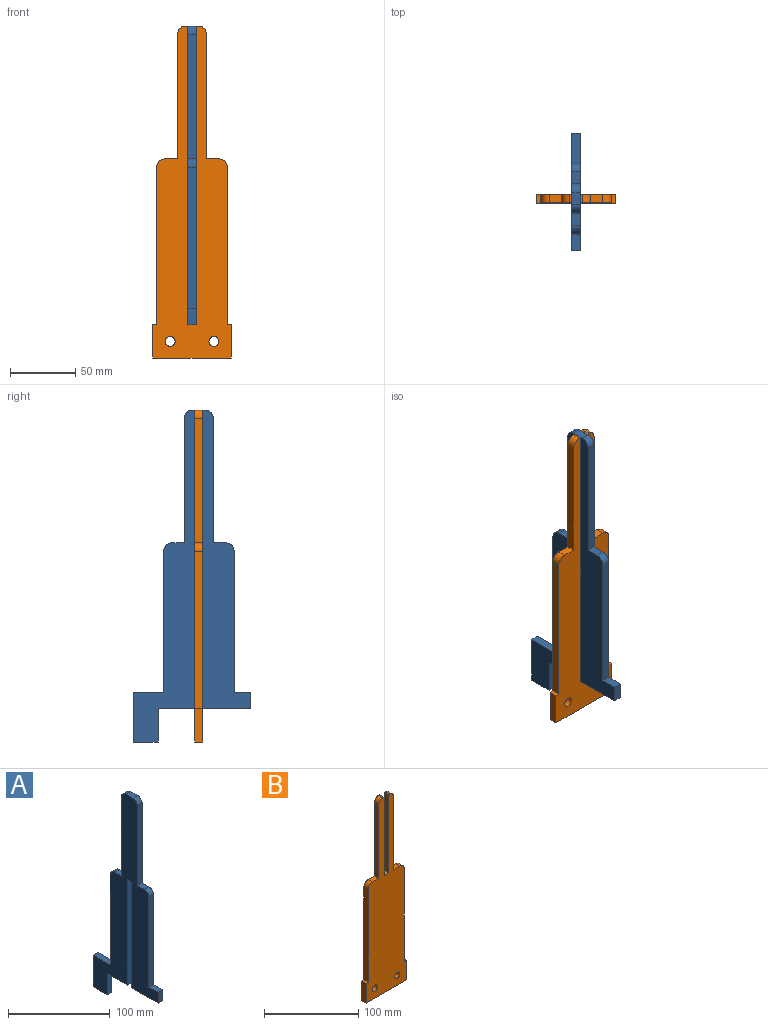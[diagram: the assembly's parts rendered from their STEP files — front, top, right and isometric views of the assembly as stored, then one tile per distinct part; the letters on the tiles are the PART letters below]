
ASSEMBLY  parts=2 mates=1
PART A: 25 faces, bbox 6.4x89.9x254 mm
  f0: plane 23.18x6.35mm, normal (0,0,1), area 147.2mm2, adj f1,f22,f23,f24
  f1: plane 107.95x6.35mm, normal (0,1,0), area 685.5mm2, adj f0,f2,f23,f24
  f2: cylinder r=6.35mm len=6.35mm, axis (-1,0,0), area 63.3mm2, adj f1,f3,f23,f24
  f3: plane 9.52x6.35mm, normal (0,0,1), area 60.5mm2, adj f2,f4,f23,f24
  f4: plane 95.25x6.35mm, normal (0,1,0), area 604.8mm2, adj f3,f5,f23,f24
  f5: cylinder r=6.35mm len=6.35mm, axis (-1,0,0), area 63.3mm2, adj f4,f6,f23,f24
  f6: plane 9.52x6.35mm, normal (0,0,1), area 60.5mm2, adj f5,f7,f23,f24
  f7: cylinder r=6.35mm len=6.35mm, axis (-1,0,0), area 63.3mm2, adj f6,f8,f23,f24
  f8: plane 95.25x6.35mm, normal (0,-1,0), area 604.8mm2, adj f7,f9,f23,f24
  f9: plane 9.54x6.35mm, normal (0,0,1), area 60.6mm2, adj f8,f10,f23,f24
  f10: cylinder r=6.35mm len=6.35mm, axis (-1,0,0), area 63.3mm2, adj f9,f11,f23,f24
  f11: plane 107.97x6.35mm, normal (0,-1,0), area 685.6mm2, adj f10,f12,f23,f24
  f12: plane 12.7x6.35mm, normal (0,0,1), area 80.6mm2, adj f11,f13,f23,f24
  f13: plane 12.7x6.35mm, normal (0,-1,0), area 80.6mm2, adj f12,f14,f23,f24
  f14: plane 12.7x6.35mm, normal (0,0,-1), area 80.6mm2, adj f13,f15,f23,f24
  f15: plane 23.81x6.35mm, normal (0,0,-1), area 151.2mm2, adj f14,f16,f23,f24
  f16: plane 127x6.35mm, normal (0,1,0), area 806.5mm2, adj f15,f17,f23,f24
  f17: plane 6.35x6.35mm, normal (0,0,-1), area 40.3mm2, adj f16,f18,f23,f24
  f18: plane 127x6.35mm, normal (0,-1,0), area 806.5mm2, adj f17,f19,f23,f24
  f19: plane 27.94x6.35mm, normal (0,0,-1), area 177.4mm2, adj f18,f20,f23,f24
  f20: plane 25.4x6.35mm, normal (0,-1,0), area 161.3mm2, adj f19,f21,f23,f24
  f21: plane 19.05x6.35mm, normal (0,0,-1), area 121mm2, adj f20,f22,f23,f24
  f22: plane 38.1x6.35mm, normal (0,1,0), area 241.9mm2, adj f0,f21,f23,f24
  f23: plane 254x89.85mm, normal (1,0,0), area 9210.6mm2, adj f0,f1,f2,f3,f4,f5,f6,f7
  f24: plane 254x89.85mm, normal (-1,0,0), area 9210.6mm2, adj f0,f1,f2,f3,f4,f5,f6,f7
PART B: 24 faces, bbox 60.3x6.4x254 mm
  f0: plane 60.33x6.35mm, normal (0,0,-1), area 383.1mm2, adj f1,f20,f22,f23
  f1: plane 25.4x6.35mm, normal (1,0,0), area 161.3mm2, adj f0,f2,f22,f23
  f2: plane 6.35x3.18mm, normal (0,0,1), area 20.2mm2, adj f1,f3,f22,f23
  f3: plane 120.65x6.35mm, normal (1,0,0), area 766.1mm2, adj f2,f4,f22,f23
  f4: cylinder r=6.35mm len=6.35mm, axis (0,1,0), area 63.3mm2, adj f3,f5,f22,f23
  f5: plane 9.53x6.35mm, normal (0,0,1), area 60.5mm2, adj f4,f6,f22,f23
  f6: plane 95.25x6.35mm, normal (1,0,0), area 604.8mm2, adj f5,f7,f22,f23
  f7: cylinder r=6.35mm len=6.35mm, axis (0,1,0), area 63.3mm2, adj f6,f8,f22,f23
  f8: plane 6.35x1.55mm, normal (0,0,1), area 9.9mm2, adj f7,f9,f22,f23
  f9: plane 101.6x6.35mm, normal (-1,0,0), area 645.2mm2, adj f8,f10,f22,f23
  f10: plane 6.35x6.31mm, normal (0,0,1), area 40.1mm2, adj f9,f11,f22,f23
  f11: plane 101.6x6.35mm, normal (1,0,0), area 645.2mm2, adj f10,f12,f22,f23
  f12: plane 6.35x1.62mm, normal (0,0,1), area 10.3mm2, adj f11,f13,f22,f23
  f13: cylinder r=6.35mm len=6.35mm, axis (0,1,0), area 63.3mm2, adj f12,f14,f22,f23
  f14: plane 95.25x6.35mm, normal (-1,0,0), area 604.8mm2, adj f13,f15,f22,f23
  f15: plane 9.53x6.35mm, normal (0,0,1), area 60.5mm2, adj f14,f16,f22,f23
  f16: cylinder r=6.35mm len=6.35mm, axis (0,1,0), area 63.3mm2, adj f15,f17,f22,f23
  f17: plane 120.65x6.35mm, normal (-1,0,0), area 766.1mm2, adj f16,f18,f22,f23
  f18: plane 6.35x3.18mm, normal (0,0,1), area 20.2mm2, adj f17,f20,f22,f23
  f19: cylinder r=3.81mm len=7.62mm, axis (0,1,0), area 152mm2, adj f22,f23
  f20: plane 25.4x6.35mm, normal (-1,0,0), area 161.3mm2, adj f0,f18,f22,f23
  f21: cylinder r=3.81mm len=7.62mm, axis (0,1,0), area 152mm2, adj f22,f23
  f22: plane 254x60.33mm, normal (0,-1,0), area 9876mm2, adj f0,f1,f2,f3,f4,f5,f6,f7
  f23: plane 254x60.33mm, normal (0,1,0), area 9876mm2, adj f0,f1,f2,f3,f4,f5,f6,f7
PLACE A t=(-19.7,23.96,22.76)mm
PLACE B t=(-19.72,23.96,-53.44)mm
MATE fastened B.f10 <-> A.f17  axis (0,0,1) through (-19.7,23.96,86.26)mm
